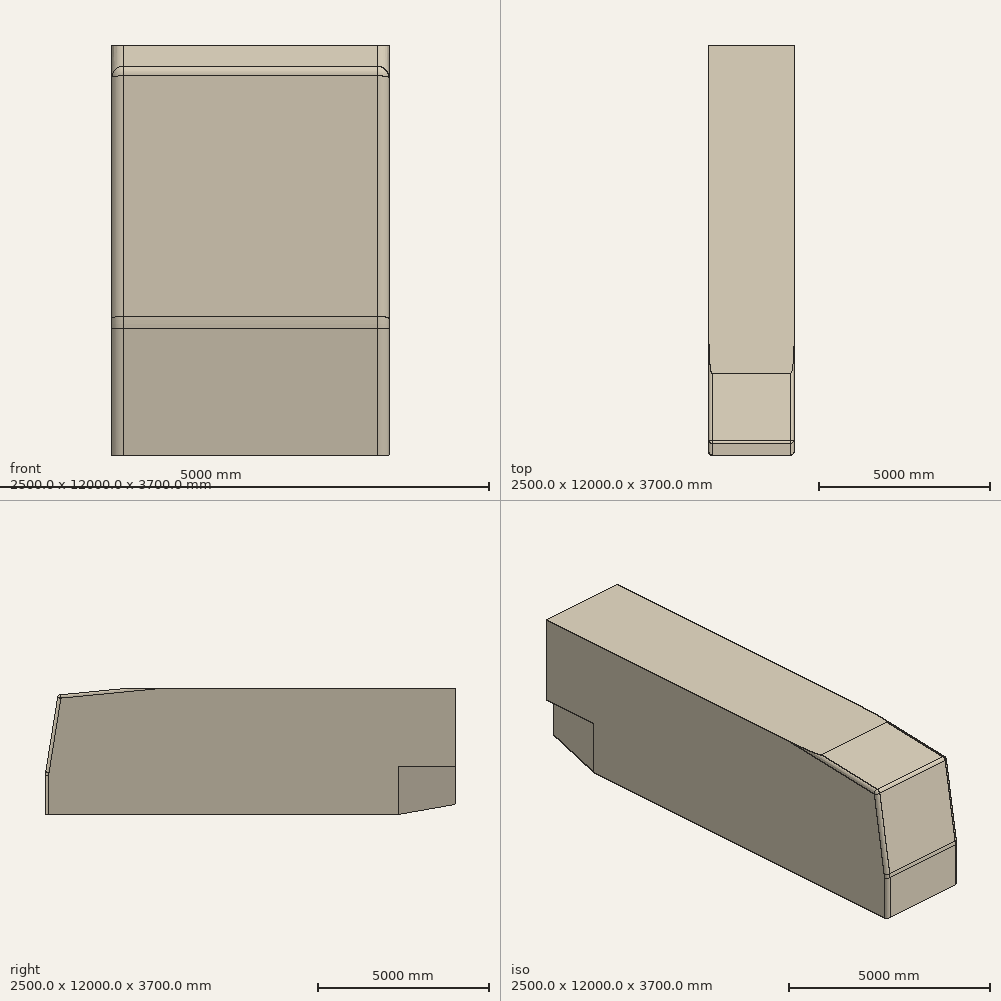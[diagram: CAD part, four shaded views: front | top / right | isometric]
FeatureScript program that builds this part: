
annotation { "Feature Type Name" : "Feature", "Feature Type Description" : "" }
export const myFeature = defineFeature(function(context is Context, id is Id, definition is map)
    precondition{}
    {
        {
            var Q0;
            Q0=qCreatedBy(makeId("Top.planeOp"),FACE);
            var sketch = newSketch(context, id + "F0", { "sketchPlane" : qUnion([Q0])});
            skLineSegment(sketch, "E0.bottom", {"start": v(-1250, 6000) * mm, "end": v(1250, 6000) * mm});
            skLineSegment(sketch, "E0.top", {"start": v(-1250, -6000) * mm, "end": v(1250, -6000) * mm});
            skLineSegment(sketch, "E0.left", {"start": v(-1250, 6000) * mm, "end": v(-1250, -6000) * mm});
            skLineSegment(sketch, "E0.right", {"start": v(1250, 6000) * mm, "end": v(1250, -6000) * mm});
            skSolve(sketch);
        }
        {
            var Q0;
            Q0=makeQuery(id+"F0.imprint","IMPRINT",FACE,{"disambiguationData":[TD([[makeQuery(id+"F0.imprint","IMPRINT",EDGE,{"derivedFrom":sQuery(id+"F0.wireOp",EDGE,"E0.bottom")}),-1.0]])]});
            extrude(context, id + "F1", {"entities" : qUnion([Q0]), "depth" : 3700 * mm, "offsetDistance" : 25 * mm});
        }
        {
            var Q0;
            Q0=makeQuery(id+"F1.opExtrude","CAP_EDGE",EDGE,{"disambiguationData":[OSD([sQuery(id+"F0.wireOp",EDGE,"E0.top")])],"isStart":false});
            chamfer(context, id + "F2", {"entities" : qUnion([Q0]), "chamferType" : ChamferType.TWO_OFFSETS, "width1" : 400 * mm, "oppositeDirection" : false, "width2" : 2500 * mm, "tangentPropagation" : true});
        }
        {
            var Q0;
            Q0=makeQuery(id+"F1.opExtrude","CAP_EDGE",EDGE,{"disambiguationData":[OSD([sQuery(id+"F0.wireOp",EDGE,"E0.bottom")])],"isStart":true});
            chamfer(context, id + "F3", {"entities" : qUnion([Q0]), "chamferType" : ChamferType.TWO_OFFSETS, "width1" : 300 * mm, "oppositeDirection" : true, "width2" : 1700 * mm, "tangentPropagation" : true});
        }
        {
            var Q0;
            {var subQ0=sQuery(id+"F0.wireOp",EDGE,"E0.top");Q0=makeQuery(id+"F2.opChamfer","BLEND_EDGE",EDGE,{"blendedFrom":[makeQuery(id+"F1.opExtrude","CAP_EDGE",EDGE,{"disambiguationData":[OSD([subQ0])],"isStart":false}),makeQuery(id+"F1.opExtrude","SWEPT_FACE",FACE,{"disambiguationData":[OSD([subQ0])]})],"blendedInto":[makeQuery(id+"F1.opExtrude","SWEPT_FACE",FACE,{"disambiguationData":[OSD([subQ0])]})]});}
            fillet(context, id + "F4", {"entities" : qUnion([Q0]), "radius" : 700 * mm, "tangentPropagation" : true, "allowEdgeOverflow" : false});
        }
        {
            var Q0;
            {var subQ0=sQuery(id+"F0.wireOp",EDGE,"E0.top");Q0=makeQuery(id+"F2.opChamfer","BLEND_EDGE",EDGE,{"blendedFrom":[makeQuery(id+"F1.opExtrude","CAP_EDGE",EDGE,{"disambiguationData":[OSD([subQ0])],"isStart":false}),makeQuery(id+"F1.opExtrude","CAP_FACE",FACE,{"disambiguationData":[OSD([sQuery(id+"F0.wireOp",EDGE,"E0.bottom"),subQ0,sQuery(id+"F0.wireOp",EDGE,"E0.left"),sQuery(id+"F0.wireOp",EDGE,"E0.right")])],"isStart":false})],"blendedInto":[makeQuery(id+"F1.opExtrude","CAP_FACE",FACE,{"disambiguationData":[OSD([sQuery(id+"F0.wireOp",EDGE,"E0.bottom"),subQ0,sQuery(id+"F0.wireOp",EDGE,"E0.left"),sQuery(id+"F0.wireOp",EDGE,"E0.right")])],"isStart":false})]});}
            chamfer(context, id + "F5", {"entities" : qUnion([Q0]), "chamferType" : ChamferType.TWO_OFFSETS, "width1" : 2000 * mm, "oppositeDirection" : false, "width2" : 200 * mm, "tangentPropagation" : true});
        }
        {
            var Q0;
            {var subQ0=sQuery(id+"F0.wireOp",EDGE,"E0.top");Q0=makeQuery(id+"F5.opChamfer","BLEND_EDGE",EDGE,{"blendedFrom":[makeQuery(id+"F2.opChamfer","BLEND_EDGE",EDGE,{"blendedFrom":[makeQuery(id+"F1.opExtrude","CAP_EDGE",EDGE,{"disambiguationData":[OSD([subQ0])],"isStart":false}),makeQuery(id+"F1.opExtrude","CAP_FACE",FACE,{"disambiguationData":[OSD([sQuery(id+"F0.wireOp",EDGE,"E0.bottom"),subQ0,sQuery(id+"F0.wireOp",EDGE,"E0.left"),sQuery(id+"F0.wireOp",EDGE,"E0.right")])],"isStart":false})],"blendedInto":[makeQuery(id+"F1.opExtrude","CAP_FACE",FACE,{"disambiguationData":[OSD([sQuery(id+"F0.wireOp",EDGE,"E0.bottom"),subQ0,sQuery(id+"F0.wireOp",EDGE,"E0.left"),sQuery(id+"F0.wireOp",EDGE,"E0.right")])],"isStart":false})]}),makeQuery(id+"F2.opChamfer","BLEND_FACE",FACE,{"disambiguationData":[OSD([subQ0])]})],"blendedInto":[makeQuery(id+"F2.opChamfer","BLEND_FACE",FACE,{"disambiguationData":[OSD([subQ0])]})]});}
            fillet(context, id + "F6", {"entities" : qUnion([Q0]), "radius" : 100 * mm, "tangentPropagation" : true, "allowEdgeOverflow" : false});
        }
        {
            var Q0;
            Q0=makeQuery(id+"F1.opExtrude","SWEPT_EDGE",EDGE,{"disambiguationData":[OSD([sQuery(id+"F0.wireOp",EDGE,"E0.top"),sQuery(id+"F0.wireOp",EDGE,"E0.left")])]});
            var Q1;
            Q1=makeQuery(id+"F2.opChamfer","BLEND_EDGE",EDGE,{"blendedFrom":[makeQuery(id+"F1.opExtrude","CAP_EDGE",EDGE,{"disambiguationData":[OSD([sQuery(id+"F0.wireOp",EDGE,"E0.top")])],"isStart":false}),makeQuery(id+"F1.opExtrude","SWEPT_FACE",FACE,{"disambiguationData":[OSD([sQuery(id+"F0.wireOp",EDGE,"E0.left")])]})],"blendedInto":[makeQuery(id+"F1.opExtrude","SWEPT_FACE",FACE,{"disambiguationData":[OSD([sQuery(id+"F0.wireOp",EDGE,"E0.left")])]})]});
            var Q2;
            Q2=makeQuery(id+"F2.opChamfer","BLEND_EDGE",EDGE,{"blendedFrom":[makeQuery(id+"F1.opExtrude","CAP_EDGE",EDGE,{"disambiguationData":[OSD([sQuery(id+"F0.wireOp",EDGE,"E0.top")])],"isStart":false}),makeQuery(id+"F1.opExtrude","SWEPT_FACE",FACE,{"disambiguationData":[OSD([sQuery(id+"F0.wireOp",EDGE,"E0.right")])]})],"blendedInto":[makeQuery(id+"F1.opExtrude","SWEPT_FACE",FACE,{"disambiguationData":[OSD([sQuery(id+"F0.wireOp",EDGE,"E0.right")])]})]});
            var Q3;
            Q3=makeQuery(id+"F1.opExtrude","SWEPT_EDGE",EDGE,{"disambiguationData":[OSD([sQuery(id+"F0.wireOp",EDGE,"E0.top"),sQuery(id+"F0.wireOp",EDGE,"E0.right")])]});
            var Q4;
            {var subQ0=sQuery(id+"F0.wireOp",EDGE,"E0.left");var subQ1=sQuery(id+"F0.wireOp",EDGE,"E0.top");Q4=makeQuery(id+"F5.opChamfer","BLEND_EDGE",EDGE,{"blendedFrom":[makeQuery(id+"F2.opChamfer","BLEND_EDGE",EDGE,{"blendedFrom":[makeQuery(id+"F1.opExtrude","CAP_EDGE",EDGE,{"disambiguationData":[OSD([subQ1])],"isStart":false}),makeQuery(id+"F1.opExtrude","CAP_FACE",FACE,{"disambiguationData":[OSD([sQuery(id+"F0.wireOp",EDGE,"E0.bottom"),subQ1,subQ0,sQuery(id+"F0.wireOp",EDGE,"E0.right")])],"isStart":false})],"blendedInto":[makeQuery(id+"F1.opExtrude","CAP_FACE",FACE,{"disambiguationData":[OSD([sQuery(id+"F0.wireOp",EDGE,"E0.bottom"),subQ1,subQ0,sQuery(id+"F0.wireOp",EDGE,"E0.right")])],"isStart":false})]}),makeQuery(id+"F1.opExtrude","SWEPT_FACE",FACE,{"disambiguationData":[OSD([subQ0])]})],"blendedInto":[makeQuery(id+"F1.opExtrude","SWEPT_FACE",FACE,{"disambiguationData":[OSD([subQ0])]})]});}
            var Q5;
            {var subQ0=sQuery(id+"F0.wireOp",EDGE,"E0.right");var subQ1=sQuery(id+"F0.wireOp",EDGE,"E0.top");Q5=makeQuery(id+"F5.opChamfer","BLEND_EDGE",EDGE,{"blendedFrom":[makeQuery(id+"F2.opChamfer","BLEND_EDGE",EDGE,{"blendedFrom":[makeQuery(id+"F1.opExtrude","CAP_EDGE",EDGE,{"disambiguationData":[OSD([subQ1])],"isStart":false}),makeQuery(id+"F1.opExtrude","CAP_FACE",FACE,{"disambiguationData":[OSD([sQuery(id+"F0.wireOp",EDGE,"E0.bottom"),subQ1,sQuery(id+"F0.wireOp",EDGE,"E0.left"),subQ0])],"isStart":false})],"blendedInto":[makeQuery(id+"F1.opExtrude","CAP_FACE",FACE,{"disambiguationData":[OSD([sQuery(id+"F0.wireOp",EDGE,"E0.bottom"),subQ1,sQuery(id+"F0.wireOp",EDGE,"E0.left"),subQ0])],"isStart":false})]}),makeQuery(id+"F1.opExtrude","SWEPT_FACE",FACE,{"disambiguationData":[OSD([subQ0])]})],"blendedInto":[makeQuery(id+"F1.opExtrude","SWEPT_FACE",FACE,{"disambiguationData":[OSD([subQ0])]})]});}
            fillet(context, id + "F7", {"entities" : qUnion([Q0, Q1, Q2, Q3, Q4, Q5]), "radius" : 100 * mm, "tangentPropagation" : true, "allowEdgeOverflow" : false});
        }
        {
            var Q0;
            Q0=makeQuery(id+"F1.opExtrude","CAP_FACE",FACE,{"disambiguationData":[OSD([sQuery(id+"F0.wireOp",EDGE,"E0.bottom"),sQuery(id+"F0.wireOp",EDGE,"E0.top"),sQuery(id+"F0.wireOp",EDGE,"E0.left"),sQuery(id+"F0.wireOp",EDGE,"E0.right")])],"isStart":true});
            var sketch = newSketch(context, id + "F8", { "sketchPlane" : qUnion([Q0])});
            skLineSegment(sketch, "E1", {"start": v(-1255, -4300) * mm, "end": v(-1255, -6005) * mm});
            skLineSegment(sketch, "E2", {"start": v(-1255, -6005) * mm, "end": v(-1000, -6005) * mm});
            skLineSegment(sketch, "E3", {"start": v(-1000, -6005) * mm, "end": v(-1255, -4300) * mm});
            skLineSegment(sketch, "E4.MirrorCS", {"start": v(1255, -6005) * mm, "end": v(1000, -6005) * mm});
            skLineSegment(sketch, "E5.MirrorCS", {"start": v(1255, -4300) * mm, "end": v(1255, -6005) * mm});
            skLineSegment(sketch, "E6.MirrorCS", {"start": v(1000, -6005) * mm, "end": v(1255, -4300) * mm});
            skSolve(sketch);
        }
        {
            var Q0;
            {var subQ5=sQuery(id+"F8.wireOp",EDGE,"E4.MirrorCS");Q0=makeQuery(id+"F8.imprint","IMPRINT",FACE,{"disambiguationData":[TD([[makeQuery(id+"F8.imprint","IMPRINT",EDGE,{"derivedFrom":subQ5}),-1.0]])]});}
            var Q1;
            {var subQ1=sQuery(id+"F8.wireOp",EDGE,"E1");Q1=makeQuery(id+"F8.imprint","IMPRINT",FACE,{"disambiguationData":[TD([[makeQuery(id+"F8.imprint","IMPRINT",EDGE,{"derivedFrom":subQ1}),1.0]])]});}
            extrude(context, id + "F9", {"entities" : qUnion([Q0, Q1]), "operationType" : NewBodyOperationType.REMOVE, "oppositeDirection" : true, "depth" : 1400 * mm, "offsetDistance" : 25 * mm});
        }
    });
